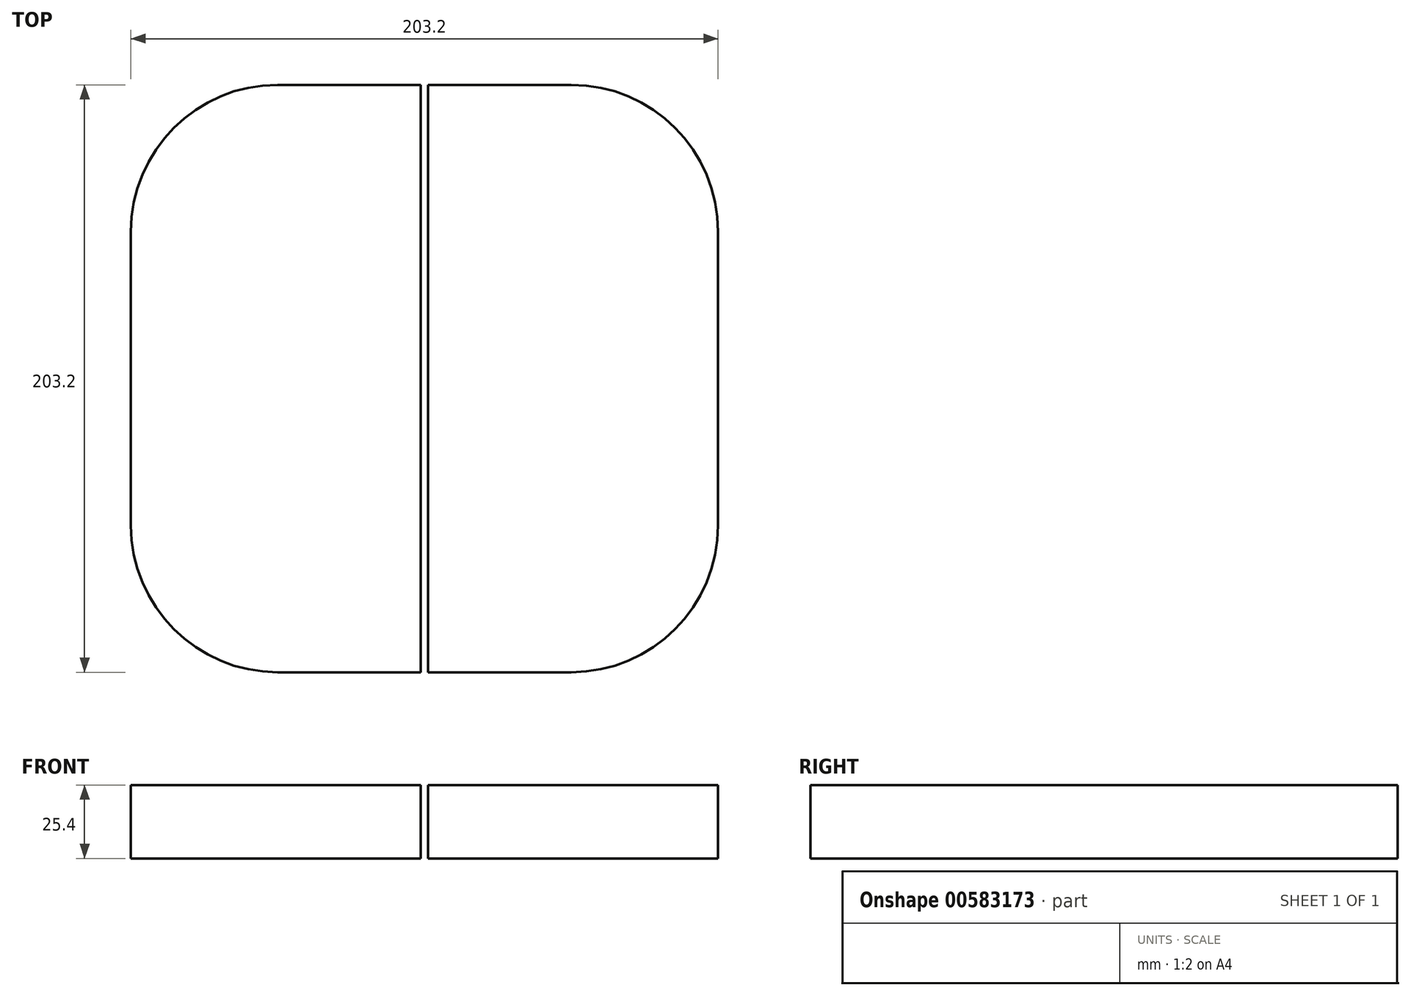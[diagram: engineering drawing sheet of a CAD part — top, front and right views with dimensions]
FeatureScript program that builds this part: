
annotation { "Feature Type Name" : "Feature", "Feature Type Description" : "" }
export const myFeature = defineFeature(function(context is Context, id is Id, definition is map)
    precondition{}
    {
        {
            var Q0;
            Q0=qCreatedBy(makeId("Top.planeOp"),FACE);
            var sketch = newSketch(context, id + "F0", { "sketchPlane" : qUnion([Q0])});
            skLineSegment(sketch, "E0.bottom", {"start": v(-116.13, 166.11) * mm, "end": v(-14.53, 166.11) * mm});
            skLineSegment(sketch, "E0.top", {"start": v(-116.13, -37.09) * mm, "end": v(-14.53, -37.09) * mm});
            skLineSegment(sketch, "E0.left", {"start": v(-166.93, 115.31) * mm, "end": v(-166.93, 13.71) * mm});
            skLineSegment(sketch, "E0.right", {"start": v(36.27, 115.31) * mm, "end": v(36.27, 13.71) * mm});
            skPoint(sketch, "E1.visualSharp", {"position": v(-166.93, 166.11) * mm});
            skArc(sketch, "E1.filletArc", {"start": v(-116.13, 166.11) * mm, "mid": v(-152.05, 151.23) * mm, "end": v(-166.93, 115.31) * mm});
            skPoint(sketch, "E2.visualSharp", {"position": v(-166.93, -37.09) * mm});
            skArc(sketch, "E2.filletArc", {"start": v(-166.93, 13.71) * mm, "mid": v(-152.05, -22.2) * mm, "end": v(-116.13, -37.09) * mm});
            skPoint(sketch, "E3.visualSharp", {"position": v(36.27, -37.09) * mm});
            skArc(sketch, "E3.filletArc", {"start": v(-14.53, -37.09) * mm, "mid": v(21.4, -22.2) * mm, "end": v(36.27, 13.71) * mm});
            skPoint(sketch, "E4.visualSharp", {"position": v(36.27, 166.11) * mm});
            skArc(sketch, "E4.filletArc", {"start": v(36.27, 115.31) * mm, "mid": v(21.4, 151.23) * mm, "end": v(-14.53, 166.11) * mm});
            skLineSegment(sketch, "E5.0", {"start": v(-66.6, 166.11) * mm, "end": v(-66.6, -37.09) * mm});
            skLineSegment(sketch, "E6.0", {"start": v(-64.06, 166.11) * mm, "end": v(-64.06, -37.09) * mm});
            skCircle(sketch, "E7", {"center": v(-116.13, 115.31) * mm, "radius": 25.4 * mm});
            skCircle(sketch, "E8", {"center": v(-14.53, 13.71) * mm, "radius": 25.4 * mm});
            skSolve(sketch);
        }
        {
            var Q0;
            Q0=makeQuery(id+"F0.imprint","IMPRINT",FACE,{"disambiguationData":[TD([[makeQuery(id+"F0.imprint","IMPRINT",EDGE,{"derivedFrom":sQuery(id+"F0.wireOp",EDGE,"E0.left")}),1.0]])]});
            var Q1;
            Q1=makeQuery(id+"F0.imprint","IMPRINT",FACE,{"disambiguationData":[TD([[makeQuery(id+"F0.imprint","IMPRINT",EDGE,{"derivedFrom":sQuery(id+"F0.wireOp",EDGE,"E0.right")}),-1.0]])]});
            var Q2;
            Q2=makeQuery(id+"F0.imprint","IMPRINT",FACE,{"disambiguationData":[TD([[makeQuery(id+"F0.imprint","IMPRINT",EDGE,{"derivedFrom":sQuery(id+"F0.wireOp",EDGE,"E7")}),1.0]])]});
            var Q3;
            Q3=makeQuery(id+"F0.imprint","IMPRINT",FACE,{"disambiguationData":[TD([[makeQuery(id+"F0.imprint","IMPRINT",EDGE,{"derivedFrom":sQuery(id+"F0.wireOp",EDGE,"E8")}),1.0]])]});
            extrude(context, id + "F1", {"entities" : qUnion([Q0, Q1, Q2, Q3]), "depth" : 25.4 * mm, "offsetDistance" : 25.4 * mm});
        }
        {
            var Q0;
            Q0=sQuery(id+"F0.wireOp",EDGE,"E7");
            extrude(context, id + "F2", {"bodyType" : ToolBodyType.SURFACE, "surfaceEntities" : qUnion([Q0]), "depth" : 25.43 * mm, "offsetDistance" : 25.4 * mm});
        }
        {
            var Q0;
            Q0=sQuery(id+"F0.wireOp",EDGE,"E8");
            extrude(context, id + "F3", {"bodyType" : ToolBodyType.SURFACE, "surfaceEntities" : qUnion([Q0]), "depth" : 25.43 * mm, "offsetDistance" : 25.4 * mm});
        }
    });
